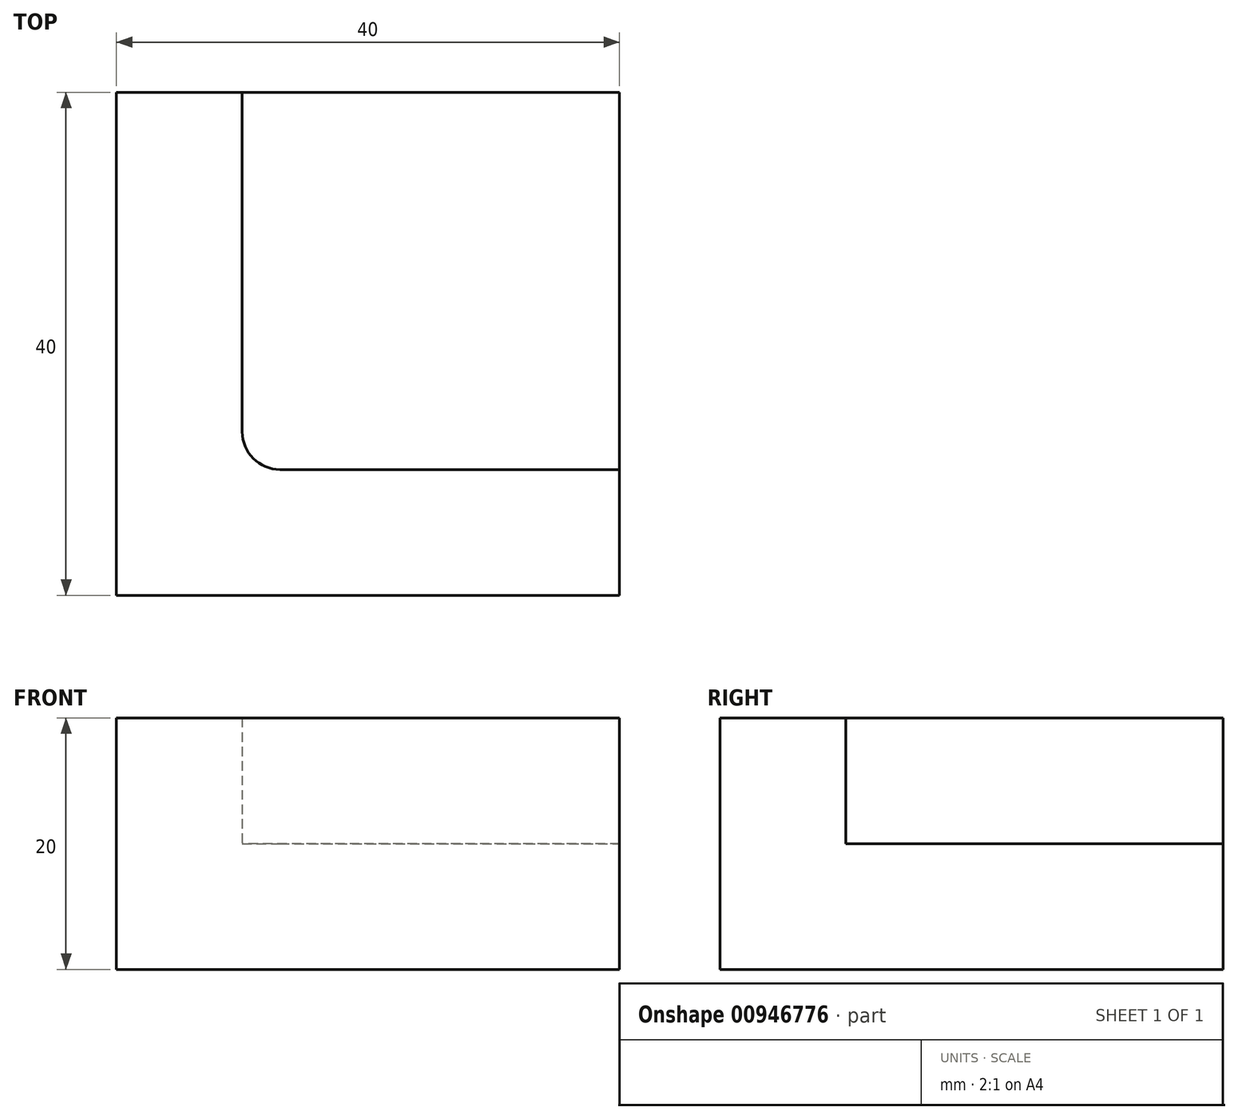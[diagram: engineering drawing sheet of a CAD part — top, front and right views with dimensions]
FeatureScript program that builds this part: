
annotation { "Feature Type Name" : "Feature", "Feature Type Description" : "" }
export const myFeature = defineFeature(function(context is Context, id is Id, definition is map)
    precondition{}
    {
        {
            var Q0;
            Q0=qCreatedBy(makeId("Top.planeOp"),FACE);
            var sketch = newSketch(context, id + "F0", { "sketchPlane" : qUnion([Q0])});
            skLineSegment(sketch, "E0.bottom", {"start": v(20, -20) * mm, "end": v(-20, -20) * mm});
            skLineSegment(sketch, "E0.top", {"start": v(20, 20) * mm, "end": v(-20, 20) * mm});
            skLineSegment(sketch, "E0.left", {"start": v(20, -20) * mm, "end": v(20, 20) * mm});
            skLineSegment(sketch, "E0.right", {"start": v(-20, -20) * mm, "end": v(-20, 20) * mm});
            skPoint(sketch, "E0.middle", {"position": v(0, 0) * mm});
            skLineSegment(sketch, "E1", {"start": v(-10, 20) * mm, "end": v(-10, -10) * mm});
            skLineSegment(sketch, "E2", {"start": v(-10, -10) * mm, "end": v(20, -10) * mm});
            skSolve(sketch);
        }
        {
            var Q0;
            {var subQ1=sQuery(id+"F0.wireOp",EDGE,"E0.bottom");Q0=makeQuery(id+"F0.imprint","IMPRINT",FACE,{"disambiguationData":[TD([[makeQuery(id+"F0.imprint","IMPRINT",EDGE,{"derivedFrom":subQ1}),-1.0]])]});}
            extrude(context, id + "F1", {"entities" : qUnion([Q0]), "depth" : 20 * mm, "offsetDistance" : 25 * mm});
        }
        {
            var Q0;
            {var subQ3=sQuery(id+"F0.wireOp",EDGE,"E1");Q0=makeQuery(id+"F0.imprint","IMPRINT",FACE,{"disambiguationData":[TD([[makeQuery(id+"F0.imprint","IMPRINT",EDGE,{"derivedFrom":subQ3}),1.0]])]});}
            extrude(context, id + "F2", {"entities" : qUnion([Q0]), "operationType" : NewBodyOperationType.ADD, "depth" : 10 * mm, "offsetDistance" : 25 * mm});
        }
        {
            var Q0;
            Q0=makeQuery(id+"F1.opExtrude","SWEPT_EDGE",EDGE,{"disambiguationData":[OSD([sQuery(id+"F0.wireOp",EDGE,"E1"),sQuery(id+"F0.wireOp",EDGE,"E2")])]});
            fillet(context, id + "F3", {"entities" : qUnion([Q0]), "radius" : 3 * mm, "tangentPropagation" : true, "allowEdgeOverflow" : false});
        }
    });
